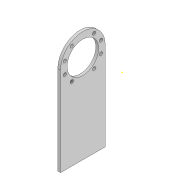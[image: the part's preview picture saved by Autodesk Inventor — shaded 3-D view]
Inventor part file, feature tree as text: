
AUTODESK INVENTOR PART (.ipt)
format: ipt  version: 2020 (Build 240168000, 168)  size: 114,688 bytes
history: native  units: in
note: dims shown in document units (in); Inventor stores cm internally (conversion verified against a paired STEP export)
features: sketch x2, extrude x1
ambient origin geometry x8: Origin, YZ Plane, XZ Plane, XY Plane, X Axis, Y Axis, Z Axis, Center Point
bodies: Solid1 (feature_tree)
feature tree (3):
  extrude  "Extrusion1"  Depth=0.2362in
  sketch  "Sketch2"  dims[d6=0.2362in d7=0.2362in d8=0.2362in d9=0.2362in d10=0.2362in d11=0.2362in d12=0.2362in d13=4.85in d14=0.1969in d15=0.0in d16=0.0394in d17=0.0394in]
  sketch  "Sketch1"  dims[d3=2.3622in d5=0.2362in]
